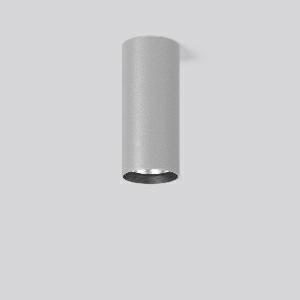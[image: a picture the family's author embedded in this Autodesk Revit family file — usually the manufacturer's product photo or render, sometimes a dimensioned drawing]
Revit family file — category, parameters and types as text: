
# Revit family: heledon_mini_a_931201_004_3_76_e9dc
name_source: partatom
category: Lighting Fixtures
units: mm (PartAtom-declared; Revit-internal decimal feet)

## family parameters
Cut with Voids When Loaded = No
Host = Face
Light Source = No
Part Type = Normal
Room Calculation Point = No
Round Connector Dimension = Use Diameter
Shared = No

## types (1)
- HELEDON mini A (1 x LED Modul 935, 2500 lm, 3500)
    Apparent Load = 20 VA
    Approval mark = CE
    CIE Flux Codes = 99 100 100 100 100
    Color Rendering = 92
    Color Temperature = 3500
    Default Elevation = 1800 mm
    Description = Series: HELEDON mini
Cylindrical surface-mounted downlight. Housing: die-cast aluminium, powder-coated. Internal ceiling frame polycarbonate with bayonet mounting. Black plastic ring and recessed LED to prevent glare from the side. Optical assembly with reflector made of MIRO-Silver with 98% total light reflection for outstanding efficiency - can be changed without tools. Best colour rendering index Ra>90. Suitable for Ceiling mounting. Easy installation with a separate ceiling frame with bayonet mounting and plug connection. Driver integrated. Connected via plug-in connector. High quality converter without flickering and stroboscopic effect. The following accessories can be mounted without use of tools: interchangeable lenses, decorative glasses, honeycomb louvre, clear and frosted diffusers, white interchangeable plastic ring. 
Colour: silver
Diameter: 87 mm
Height: 197 mm
Lamp: LED
Socket: without socket
Colour temperature: 3500K
Colour rendering index (CRI): 92
System power: 20 W
Rated luminous flux: 2500 lm
Luminous efficiency: 125 lm/W
Control gear: Converter, dimmable, DALI
Protection class: I
Type of protection: IP 20
    Height = 197 mm
    Lamp = 1 x LED Modul 935
    Lamp Light Flux = 2500 lm
    Lamp count = 1
    Length = 87 mm
    Lifetime = 50000 h
    Luminous efficacy = 125 lm/W
    Manufacturer = RZB
    ModVariant = No
    Model = 931201.004.3.76
    Mounting Place = Ceiling
    Mounting Type = Surface mounted
    Number of Poles = 1
    OnlyDefault = Yes
    Power Factor = 1
    Product Name = HELEDON mini A
    Product group = Surface mounted downlights
    ProductGroupID = 302
    Protection Class = Protection class I
    Protection Degree = IP 20
    RLX_Detail_Level = 1
    RLX_Emergency_Light_Flux = 0 lm
    RLX_Emergency_Type = 0
    RLX_Emergency_Type_DB = No
    RlxData = <blob elided: 105565 chars, md5=3a8f745f>
    Socket = socket
    Standby Power = 0 W
    System Light Flux = 2500 lm
    System Power = 20 W
    Type Comments = Product without accessories
    Type Image = 931188.004.jpg
    URL = http://relux.com
    VarID = ---
    Voltage = 230 V
    Voltage Range = 220-240 V
    Weight = 0.00 kg
    Width = 0 mm  [stored 0 ft]

note: [stored X ft] marks values corroborated as IEEE doubles in the binary element streams (Revit-internal decimal feet)

## geometry (parser evidence)
native form markers: Blend x4, Sweep x7
no freeform markers — native parametric forms only
